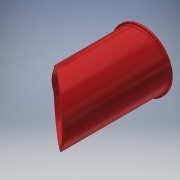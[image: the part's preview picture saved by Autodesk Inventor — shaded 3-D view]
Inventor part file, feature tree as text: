
AUTODESK INVENTOR PART (.ipt)
format: ipt  version: 2017.3 (Build 213257000, 257)  size: 156,672 bytes
history: native  units: in
note: dims shown in document units (in); Inventor stores cm internally (conversion verified against a paired STEP export)
features: extrude x5, sketch x5, fillet x2, chamfer x1
ambient origin geometry x8: Origin, YZ Plane, XZ Plane, XY Plane, X Axis, Y Axis, Z Axis, Center Point
bodies: Solid1 (feature_tree)
feature tree (13):
  extrude  "Extrusion1"  Depth=1.0in TaperAngle=0.0deg
  extrude  "Extrusion2"  Depth=1.9685in TaperAngle=0.0deg
  extrude  "Extrusion3"  Depth=52.391in TaperAngle=0.0deg
  extrude  "Extrusion4"  Depth=0.0312in TaperAngle=0.0deg
  chamfer  "Chamfer1"  Distance=0.0312in Angle=45.0deg
  fillet  "Fillet1"  Radius=0.0312in
  fillet  "Fillet2"  Radius=0.0312in
  extrude  "Extrusion5"  Depth=1.0in TaperAngle=0.0deg
  sketch  "Sketch1"  dims[d0=29.52in d1=1.0in d2=0.0in]
  sketch  "Sketch2"  dims[d3=28.02in d4=1.9685in d5=0.0in]
  sketch  "Sketch3"  dims[d6=27.5in d7=52.391in d8=0.0in]
  sketch  "Sketch4"  dims[d9=25.0in d11=30.9055in d12=0.0in d13=0.0312in d14=0.125in d15=45.0deg d16=0.0312in d17=0.0312in]
  sketch  "Sketch5"  dims[d18=0.2749in d19=1.0in d20=0.0in d21=0.25in]
